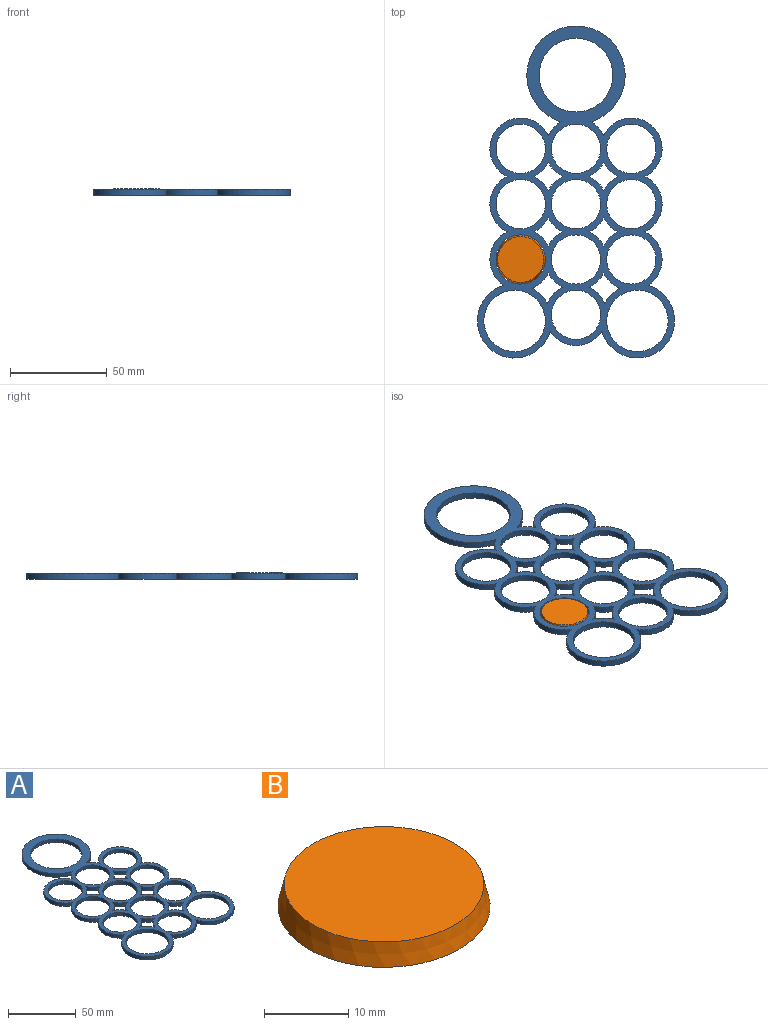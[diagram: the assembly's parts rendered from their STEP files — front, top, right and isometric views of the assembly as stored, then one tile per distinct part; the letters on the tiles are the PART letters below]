
ASSEMBLY  parts=2 mates=1
PART A: 51 faces, bbox 101.9x171.7x3.2 mm
  f0: plane 171.67x101.91mm, normal (0,0,1), area 3953.6mm2, adj f2,f3,f4,f5,f6,f7,f8,f9
  f1: plane 171.67x101.91mm, normal (0,0,-1), area 3953.6mm2, adj f2,f3,f4,f5,f6,f7,f8,f9
  f2: cylinder r=12.7mm len=25.4mm, axis (0,0,-1), area 253.4mm2, adj f0,f1
  f3: cylinder r=12.7mm len=25.4mm, axis (0,0,-1), area 253.4mm2, adj f0,f1
  f4: cylinder r=12.7mm len=25.4mm, axis (0,0,-1), area 253.4mm2, adj f0,f1
  f5: cylinder r=12.7mm len=25.4mm, axis (0,0,-1), area 253.4mm2, adj f0,f1
  f6: cylinder r=12.7mm len=25.4mm, axis (0,0,-1), area 253.4mm2, adj f0,f1
  f7: cylinder r=12.7mm len=25.4mm, axis (0,0,-1), area 253.4mm2, adj f0,f1
  f8: cylinder r=12.7mm len=25.4mm, axis (0,0,-1), area 253.4mm2, adj f0,f1
  f9: cylinder r=12.7mm len=25.4mm, axis (0,0,-1), area 253.4mm2, adj f0,f1
  f10: cylinder r=12.7mm len=25.4mm, axis (0,0,-1), area 253.4mm2, adj f0,f1
  f11: cylinder r=12.7mm len=25.4mm, axis (0,0,-1), area 253.4mm2, adj f0,f1
  f12: cylinder r=15.88mm len=31.75mm, axis (0,0,-1), area 316.7mm2, adj f0,f1
  f13: cylinder r=15.88mm len=31.75mm, axis (0,0,-1), area 316.7mm2, adj f0,f1
  f14: cylinder r=19.05mm len=38.1mm, axis (0,0,-1), area 380mm2, adj f0,f1
  f15: cylinder r=15.91mm len=7.34mm, axis (0,0,1), area 33.6mm2, adj f0,f1,f16,f18
  f16: cylinder r=15.91mm len=8.44mm, axis (0,0,1), area 37.4mm2, adj f0,f1,f15,f17
  f17: cylinder r=19.2mm len=7.96mm, axis (0,0,1), area 36.3mm2, adj f0,f1,f16,f18
  f18: cylinder r=15.9mm len=8.44mm, axis (0,0,1), area 37.4mm2, adj f0,f1,f15,f17
  f19: cylinder r=15.91mm len=7.34mm, axis (0,0,1), area 33.5mm2, adj f0,f1,f20,f22
  f20: cylinder r=15.91mm len=7.34mm, axis (0,0,1), area 33.5mm2, adj f0,f1,f19,f21
  f21: cylinder r=15.91mm len=7.34mm, axis (0,0,1), area 33.5mm2, adj f0,f1,f20,f22
  f22: cylinder r=15.91mm len=7.34mm, axis (0,0,1), area 33.5mm2, adj f0,f1,f19,f21
  f23: cylinder r=15.91mm len=6.94mm, axis (0,0,1), area 30.8mm2, adj f0,f1,f24,f34
  f24: cylinder r=15.91mm len=30.22mm, axis (0,0,1), area 192.2mm2, adj f0,f1,f23,f25
  f25: cylinder r=15.91mm len=28.61mm, axis (0,0,1), area 112.9mm2, adj f0,f1,f24,f26
  f26: cylinder r=15.91mm len=27.66mm, axis (0,0,1), area 106.8mm2, adj f0,f1,f25,f27
  f27: cylinder r=19.2mm len=37.61mm, axis (0,0,1), area 251.9mm2, adj f0,f1,f26,f28
  f28: cylinder r=15.9mm len=26.69mm, axis (0,0,1), area 100.6mm2, adj f0,f1,f27,f29
  f29: cylinder r=19.2mm len=37.61mm, axis (0,0,1), area 251.9mm2, adj f0,f1,f28,f30
  f30: cylinder r=15.91mm len=27.66mm, axis (0,0,1), area 106.8mm2, adj f0,f1,f29,f31
  f31: cylinder r=15.9mm len=28.59mm, axis (0,0,1), area 112.9mm2, adj f0,f1,f30,f32
  f32: cylinder r=15.91mm len=30.22mm, axis (0,0,1), area 192.3mm2, adj f0,f1,f31,f33
  f33: cylinder r=15.91mm len=6.94mm, axis (0,0,1), area 30.8mm2, adj f0,f1,f32,f34
  f34: cylinder r=25.4mm len=50.8mm, axis (0,0,1), area 456.8mm2, adj f0,f1,f23,f33
  f35: cylinder r=15.91mm len=7.34mm, axis (0,0,1), area 33.6mm2, adj f0,f1,f36,f38
  f36: cylinder r=15.9mm len=8.44mm, axis (0,0,1), area 37.4mm2, adj f0,f1,f35,f37
  f37: cylinder r=19.2mm len=7.96mm, axis (0,0,1), area 36.3mm2, adj f0,f1,f36,f38
  f38: cylinder r=15.91mm len=8.44mm, axis (0,0,1), area 37.4mm2, adj f0,f1,f35,f37
  f39: cylinder r=15.91mm len=7.34mm, axis (0,0,1), area 33.6mm2, adj f0,f1,f40,f42
  f40: cylinder r=15.91mm len=7.34mm, axis (0,0,1), area 33.6mm2, adj f0,f1,f39,f41
  f41: cylinder r=15.91mm len=7.34mm, axis (0,0,1), area 33.6mm2, adj f0,f1,f40,f42
  f42: cylinder r=15.91mm len=7.34mm, axis (0,0,1), area 33.6mm2, adj f0,f1,f39,f41
  f43: cylinder r=15.91mm len=7.35mm, axis (0,0,1), area 33.6mm2, adj f0,f1,f44,f46
  f44: cylinder r=15.91mm len=7.34mm, axis (0,0,1), area 33.5mm2, adj f0,f1,f43,f45
  f45: cylinder r=15.91mm len=7.34mm, axis (0,0,1), area 33.6mm2, adj f0,f1,f44,f46
  f46: cylinder r=15.9mm len=7.34mm, axis (0,0,1), area 33.6mm2, adj f0,f1,f43,f45
  f47: cylinder r=15.91mm len=7.34mm, axis (0,0,1), area 33.6mm2, adj f0,f1,f48,f50
  f48: cylinder r=15.91mm len=7.35mm, axis (0,0,1), area 33.6mm2, adj f0,f1,f47,f49
  f49: cylinder r=15.9mm len=7.35mm, axis (0,0,1), area 33.6mm2, adj f0,f1,f48,f50
  f50: cylinder r=15.91mm len=7.35mm, axis (0,0,1), area 33.6mm2, adj f0,f1,f47,f49
PART B: 5 faces, bbox 25.1x25.1x3.2 mm
  f0: cone r=12.57mm half-angle=13deg, axis (0,0,-1), area 249.9mm2, adj f1,f2
  f1: plane 23.68x23.68mm, normal (0,0,1), area 440.4mm2, adj f0
  f2: plane 25.15x25.15mm, normal (0,0,-1), area 120.4mm2, adj f0,f3
  f3: cone r=11.03mm half-angle=13deg, axis (0,0,-1), area 110.2mm2, adj f2,f4
  f4: plane 21.15x21.15mm, normal (0,0,-1), area 351.5mm2, adj f3
PLACE A t=(0.13,-0.22,0)mm fixed
PLACE B t=(0.13,-0.22,0.22)mm
MATE slider B.f0 <-> A.f2  axis (0,0,-1) through (0.13,-0.22,0.22)mm
